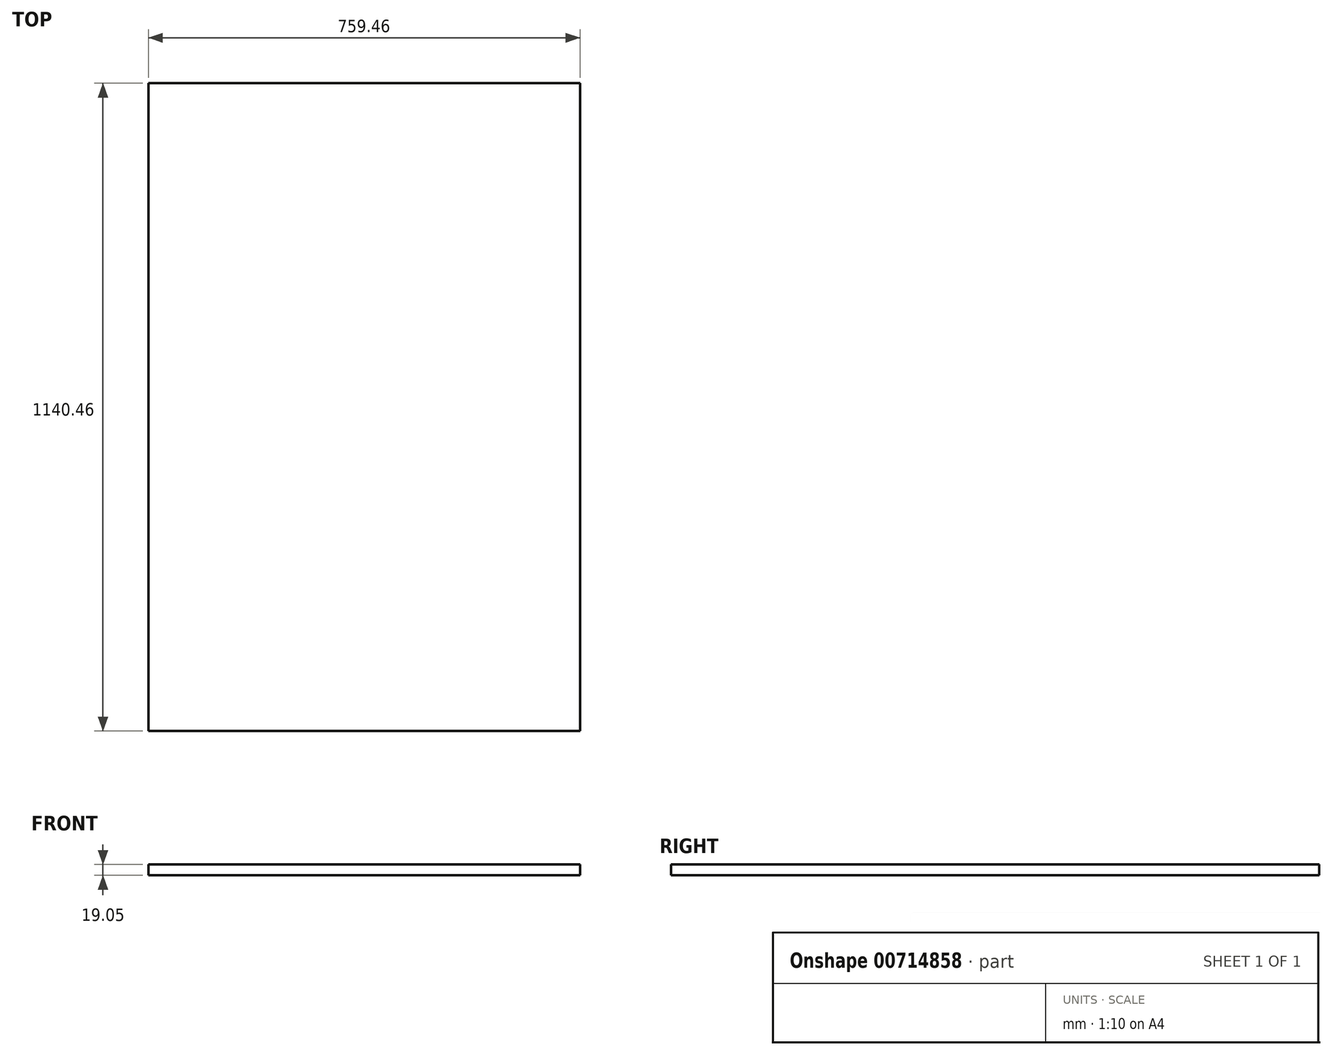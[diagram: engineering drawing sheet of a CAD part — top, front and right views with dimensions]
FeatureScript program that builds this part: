
annotation { "Feature Type Name" : "Feature", "Feature Type Description" : "" }
export const myFeature = defineFeature(function(context is Context, id is Id, definition is map)
    precondition{}
    {
        {
            var Q0;
            Q0=qCreatedBy(makeId("Top.planeOp"),FACE);
            var sketch = newSketch(context, id + "F0", { "sketchPlane" : qUnion([Q0])});
            skLineSegment(sketch, "E0.bottom", {"start": v(379.73, 570.23) * mm, "end": v(-379.73, 570.23) * mm});
            skLineSegment(sketch, "E0.top", {"start": v(379.73, -570.23) * mm, "end": v(-379.73, -570.23) * mm});
            skLineSegment(sketch, "E0.left", {"start": v(379.73, 570.23) * mm, "end": v(379.73, -570.23) * mm});
            skLineSegment(sketch, "E0.right", {"start": v(-379.73, 570.23) * mm, "end": v(-379.73, -570.23) * mm});
            skPoint(sketch, "E0.middle", {"position": v(0, 0) * mm});
            skSolve(sketch);
        }
        {
            var Q0;
            Q0 = qSketchRegion(id + "F0", true);
            extrude(context, id + "F1", {"entities" : qUnion([Q0]), "depth" : 19.05 * mm, "offsetDistance" : 25.4 * mm});
        }
    });
